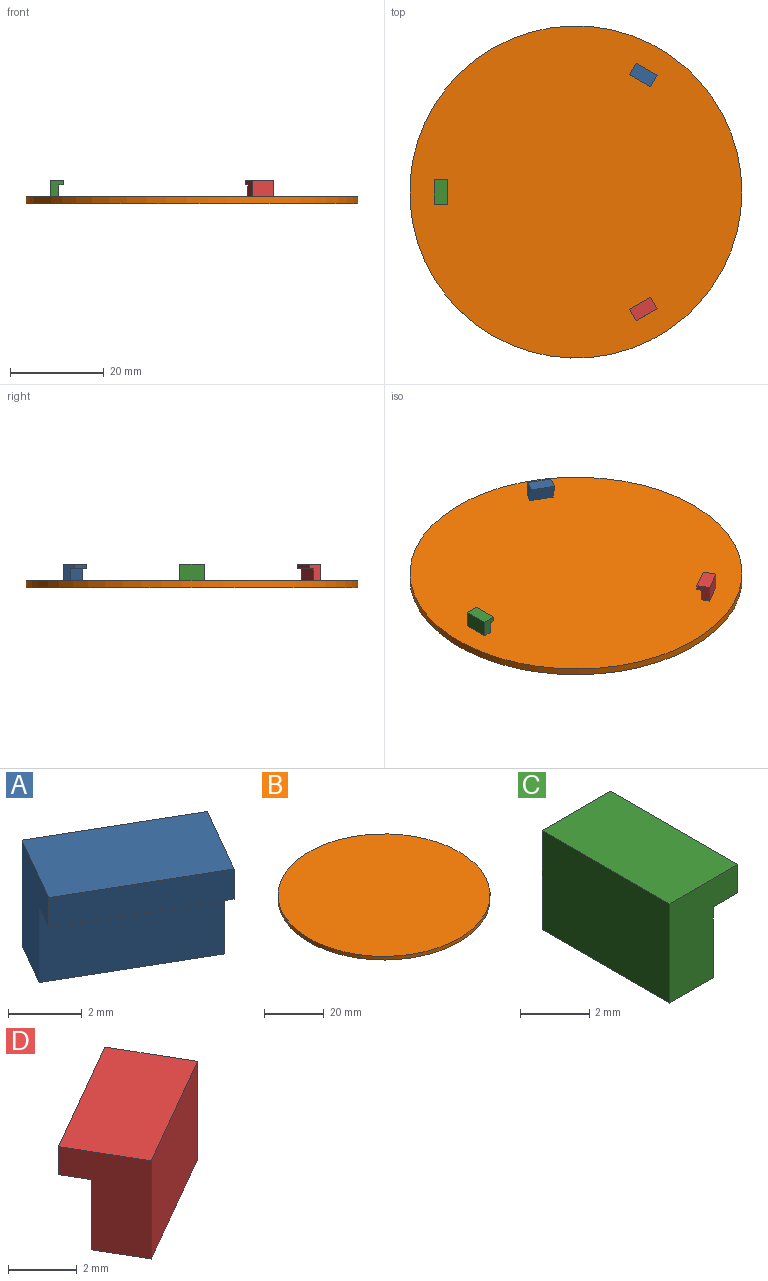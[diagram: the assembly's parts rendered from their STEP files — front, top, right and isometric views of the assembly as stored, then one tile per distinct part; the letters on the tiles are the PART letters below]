
ASSEMBLY  parts=4 mates=3
PART A: 8 faces, bbox 5.9x5x3.5 mm
  f0: plane 4.5x2.6mm, normal (-0.5,-0.87,0), area 13mm2, adj f1,f3,f5,f7
  f1: plane 3.5x2.43mm, normal (0.87,-0.5,0), area 7.3mm2, adj f0,f2,f4,f5,f6,f7
  f2: plane 4.5x3.5mm, normal (0.5,0.87,0), area 18.2mm2, adj f1,f3,f4,f5
  f3: plane 3.5x2.43mm, normal (-0.87,0.5,0), area 7.3mm2, adj f0,f2,f4,f5,f6,f7
  f4: plane 5.9x5.03mm, normal (0,0,1), area 14.6mm2, adj f1,f2,f3,f6
  f5: plane 5.4x4.16mm, normal (0,0,-1), area 9.4mm2, adj f0,f1,f2,f3
  f6: plane 4.5x2.6mm, normal (-0.5,-0.87,0), area 5.2mm2, adj f1,f3,f4,f7
  f7: plane 5x3.47mm, normal (0,0,-1), area 5.2mm2, adj f0,f1,f3,f6
PART B: 3 faces, bbox 71x71x1.5 mm
  f0: cylinder r=35.5mm len=71mm, axis (0,0,-1), area 334.6mm2, adj f1,f2
  f1: plane 71x71mm, normal (0,0,1), area 3959.2mm2, adj f0
  f2: plane 71x71mm, normal (0,0,-1), area 3959.2mm2, adj f0
PART C: 8 faces, bbox 2.8x5.2x3.5 mm
  f0: plane 5.2x2.5mm, normal (1,0,0), area 13mm2, adj f1,f2,f5,f7
  f1: plane 3.5x2.8mm, normal (0,-1,0), area 7.3mm2, adj f0,f3,f4,f5,f6,f7
  f2: plane 3.5x2.8mm, normal (0,1,0), area 7.3mm2, adj f0,f3,f4,f5,f6,f7
  f3: plane 5.2x3.5mm, normal (-1,0,0), area 18.2mm2, adj f1,f2,f4,f5
  f4: plane 5.2x2.8mm, normal (0,0,1), area 14.6mm2, adj f1,f2,f3,f6
  f5: plane 5.2x1.8mm, normal (0,0,-1), area 9.4mm2, adj f0,f1,f2,f3
  f6: plane 5.2x1mm, normal (1,0,0), area 5.2mm2, adj f1,f2,f4,f7
  f7: plane 5.2x1mm, normal (0,0,-1), area 5.2mm2, adj f0,f1,f2,f6
PART D: 8 faces, bbox 5.9x5x3.5 mm
  f0: plane 4.5x2.6mm, normal (-0.5,0.87,0), area 13mm2, adj f1,f3,f5,f7
  f1: plane 3.5x2.43mm, normal (-0.87,-0.5,0), area 7.3mm2, adj f0,f2,f4,f5,f6,f7
  f2: plane 4.5x3.5mm, normal (0.5,-0.87,0), area 18.2mm2, adj f1,f3,f4,f5
  f3: plane 3.5x2.43mm, normal (0.87,0.5,0), area 7.3mm2, adj f0,f2,f4,f5,f6,f7
  f4: plane 5.9x5.03mm, normal (0,0,1), area 14.6mm2, adj f1,f2,f3,f6
  f5: plane 5.4x4.16mm, normal (0,0,-1), area 9.4mm2, adj f0,f1,f2,f3
  f6: plane 4.5x2.6mm, normal (-0.5,0.87,0), area 5.2mm2, adj f1,f3,f4,f7
  f7: plane 5x3.47mm, normal (0,0,-1), area 5.2mm2, adj f0,f1,f3,f6
PLACE A t=(0.72,0.54,-1.31)mm
PLACE B rot(axis=(0,1,0),0deg) t=(0.72,0.54,-2.81)mm
PLACE C t=(0.72,0.54,-1.31)mm
PLACE D t=(0.72,0.54,-1.31)mm
MATE fastened D.f5 <-> A.f5  axis (0,0,1) through (0.72,0.54,-1.31)mm
MATE fastened B.f0 <-> C.f5  axis (0,0,1) through (0.72,0.54,-1.31)mm
MATE fastened C.f5 <-> D.f5  axis (0,0,1) through (0.72,0.54,-1.31)mm
